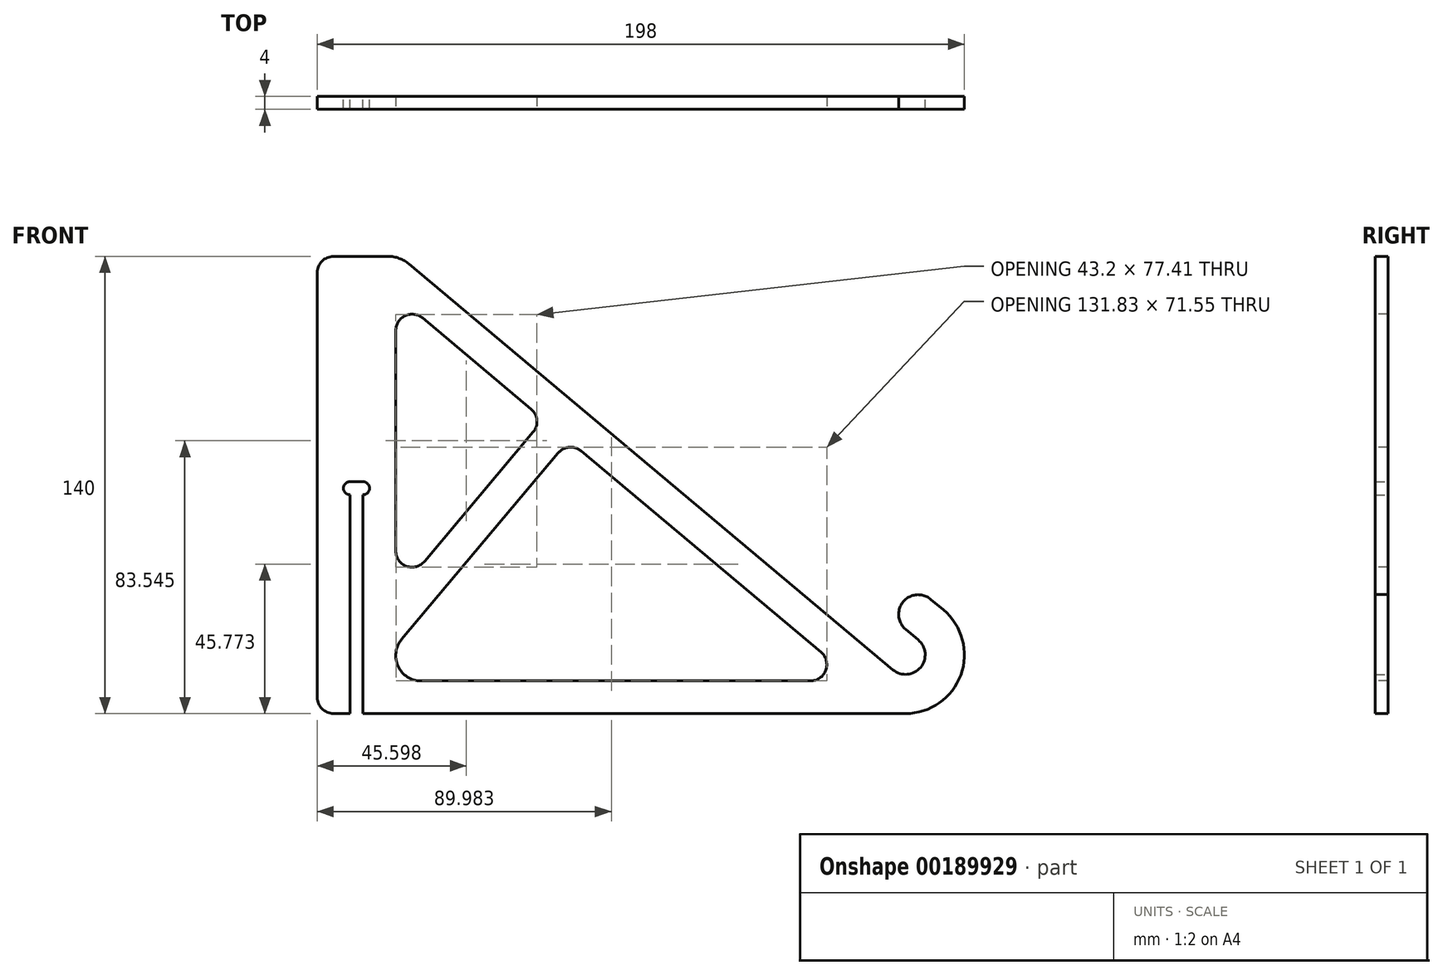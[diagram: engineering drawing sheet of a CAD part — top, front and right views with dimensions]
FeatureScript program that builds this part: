
annotation { "Feature Type Name" : "Feature", "Feature Type Description" : "" }
export const myFeature = defineFeature(function(context is Context, id is Id, definition is map)
    precondition{}
    {
        {
            var Q0;
            Q0=qCreatedBy(makeId("Front.planeOp"),FACE);
            var sketch = newSketch(context, id + "F0", { "sketchPlane" : qUnion([Q0])});
            skArc(sketch, "E0", {"start": v(-3.86, -4.6) * mm, "mid": v(4.6, -3.86) * mm, "end": v(3.86, 4.6) * mm});
            skLineSegment(sketch, "E1", {"start": v(3.86, 4.6) * mm, "end": v(0.03, 7.81) * mm});
            skArc(sketch, "E2", {"start": v(7.74, 17) * mm, "mid": v(-0.71, 16.26) * mm, "end": v(0.03, 7.81) * mm});
            skLineSegment(sketch, "E3", {"start": v(7.74, 17) * mm, "end": v(11.57, 13.79) * mm});
            skArc(sketch, "E4", {"start": v(0, -18) * mm, "mid": v(16.91, -6.16) * mm, "end": v(11.57, 13.79) * mm});
            skLineSegment(sketch, "E5", {"start": v(0, -18) * mm, "end": v(-166, -18) * mm});
            skLineSegment(sketch, "E6", {"start": v(-3.86, -4.6) * mm, "end": v(-151.94, 119.66) * mm});
            skLineSegment(sketch, "E7", {"start": v(-180, -13) * mm, "end": v(-180, 117) * mm});
            skLineSegment(sketch, "E8", {"start": v(-175, 122) * mm, "end": v(-175, 122) * mm});
            skPoint(sketch, "E9.visualSharp", {"position": v(-154.73, 122) * mm});
            skArc(sketch, "E9.filletArc", {"start": v(-151.94, 119.66) * mm, "mid": v(-154.95, 121.4) * mm, "end": v(-158.37, 122) * mm});
            skPoint(sketch, "E10.visualSharp", {"position": v(-180, 122) * mm});
            skArc(sketch, "E10.filletArc", {"start": v(-175, 122) * mm, "mid": v(-178.54, 120.54) * mm, "end": v(-180, 117) * mm});
            skPoint(sketch, "E11.visualSharp", {"position": v(-180, -18) * mm});
            skArc(sketch, "E11.filletArc", {"start": v(-180, -13) * mm, "mid": v(-178.54, -16.54) * mm, "end": v(-175, -18) * mm});
            skLineSegment(sketch, "E12.trimOffspring", {"start": v(-151.94, 119.66) * mm, "end": v(-151.94, 119.66) * mm});
            skLineSegment(sketch, "E13.trimOffspring", {"start": v(-175, 122) * mm, "end": v(-158.37, 122) * mm});
            skLineSegment(sketch, "E14", {"start": v(-170, -18) * mm, "end": v(-170, 49) * mm});
            skLineSegment(sketch, "E15", {"start": v(-170, 53) * mm, "end": v(-166, 53) * mm});
            skArc(sketch, "E16", {"start": v(-170, 53) * mm, "mid": v(-172, 51) * mm, "end": v(-170, 49) * mm});
            skArc(sketch, "E17", {"start": v(-166, 49) * mm, "mid": v(-164, 51) * mm, "end": v(-166, 53) * mm});
            skLineSegment(sketch, "E18.trimOffspring", {"start": v(-166, 49) * mm, "end": v(-166, -18) * mm});
            skLineSegment(sketch, "E19.trimOffspring", {"start": v(-170, -18) * mm, "end": v(-175, -18) * mm});
            skSolve(sketch);
        }
        {
            var Q0;
            Q0=makeQuery(id+"F0.imprint","IMPRINT",FACE,{"disambiguationData":[TD([[makeQuery(id+"F0.imprint","IMPRINT",EDGE,{"derivedFrom":sQuery(id+"F0.wireOp",EDGE,"E0")}),-1.0]])]});
            extrude(context, id + "F1", {"entities" : qUnion([Q0]), "depth" : 4 * mm, "symmetric" : true});
        }
        {
            var Q0;
            Q0=makeQuery(id+"F1.opExtrude","CAP_FACE",FACE,{"disambiguationData":[OSD([sQuery(id+"F0.wireOp",EDGE,"E0"),sQuery(id+"F0.wireOp",EDGE,"E1"),sQuery(id+"F0.wireOp",EDGE,"E2"),sQuery(id+"F0.wireOp",EDGE,"E3"),sQuery(id+"F0.wireOp",EDGE,"E4"),sQuery(id+"F0.wireOp",EDGE,"E5"),sQuery(id+"F0.wireOp",EDGE,"E6"),sQuery(id+"F0.wireOp",EDGE,"E7"),sQuery(id+"F0.wireOp",EDGE,"E9.filletArc"),sQuery(id+"F0.wireOp",EDGE,"E10.filletArc"),sQuery(id+"F0.wireOp",EDGE,"E11.filletArc"),sQuery(id+"F0.wireOp",EDGE,"KKBbhiON-uZGm-shyD-xdfM-IBxyFgNXndBr"),sQuery(id+"F0.wireOp",EDGE,"XV1xRKOV-hTZa-60WU-BiPw-Yr6rwe2VKIiS"),sQuery(id+"F0.wireOp",EDGE,"E13.trimOffspring"),sQuery(id+"F0.wireOp",EDGE,"5e8b0b0e-66d4-421e-9100-8b92fc022138.filletArc"),sQuery(id+"F0.wireOp",EDGE,"qYwrquJc-JBTd-BDjn-q7b8-VyQuV4tnNDMF"),sQuery(id+"F0.wireOp",EDGE,"uKorWGqi-1RaI-lkkf-aG7Y-YXAiGeQvXDSx"),sQuery(id+"F0.wireOp",EDGE,"a34cbe0f-19c3-4e52-acef-b7e6812299df.trimOffspring"),sQuery(id+"F0.wireOp",EDGE,"3f6b7245-64b9-41c0-b42b-52e41c2081db.filletArc")])],"isStart":false});
            var sketch = newSketch(context, id + "F2", { "sketchPlane" : qUnion([Q0])});
            skLineSegment(sketch, "E20", {"start": v(-100.48, 76.48) * mm, "end": v(-178.54, -16.54) * mm, "construction": true});
            skLineSegment(sketch, "E21", {"start": v(-147.79, 103.12) * mm, "end": v(-114.57, 75.25) * mm});
            skLineSegment(sketch, "E22", {"start": v(-113.96, 68.2) * mm, "end": v(-147.17, 28.62) * mm});
            skLineSegment(sketch, "E23", {"start": v(-156, 31.84) * mm, "end": v(-156, 99.3) * mm});
            skLineSegment(sketch, "E24", {"start": v(-99.25, 62.4) * mm, "end": v(-25.88, 0.83) * mm});
            skLineSegment(sketch, "E25", {"start": v(-29.1, -8) * mm, "end": v(-148.27, -8) * mm});
            skLineSegment(sketch, "E26", {"start": v(-154.2, 4.7) * mm, "end": v(-106.3, 61.78) * mm});
            skPoint(sketch, "E27.visualSharp", {"position": v(-156, 110.01) * mm});
            skArc(sketch, "E27.filletArc", {"start": v(-147.79, 103.12) * mm, "mid": v(-153.11, 103.82) * mm, "end": v(-156, 99.3) * mm});
            skPoint(sketch, "E28.visualSharp", {"position": v(-110.74, 72.04) * mm});
            skArc(sketch, "E28.filletArc", {"start": v(-113.96, 68.2) * mm, "mid": v(-112.8, 71.86) * mm, "end": v(-114.57, 75.25) * mm});
            skPoint(sketch, "E29.visualSharp", {"position": v(-156, 18.1) * mm});
            skArc(sketch, "E29.filletArc", {"start": v(-156, 31.84) * mm, "mid": v(-152.71, 27.14) * mm, "end": v(-147.17, 28.62) * mm});
            skPoint(sketch, "E30.visualSharp", {"position": v(-103.08, 65.6) * mm});
            skArc(sketch, "E30.filletArc", {"start": v(-99.25, 62.4) * mm, "mid": v(-102.9, 63.55) * mm, "end": v(-106.3, 61.78) * mm});
            skPoint(sketch, "E31.visualSharp", {"position": v(-15.36, -8) * mm});
            skArc(sketch, "E31.filletArc", {"start": v(-29.1, -8) * mm, "mid": v(-24.4, -4.71) * mm, "end": v(-25.88, 0.83) * mm});
            skArc(sketch, "E32", {"start": v(-154.2, 4.7) * mm, "mid": v(-155.28, -3.54) * mm, "end": v(-148.27, -8) * mm});
            skSolve(sketch);
        }
        {
            var Q0;
            Q0 = qSketchRegion(id + "F2", true);
            extrude(context, id + "F3", {"entities" : qUnion([Q0]), "operationType" : NewBodyOperationType.REMOVE, "endBound" : BoundingType.THROUGH_ALL, "oppositeDirection" : true, "depth" : 25 * mm});
        }
    });
